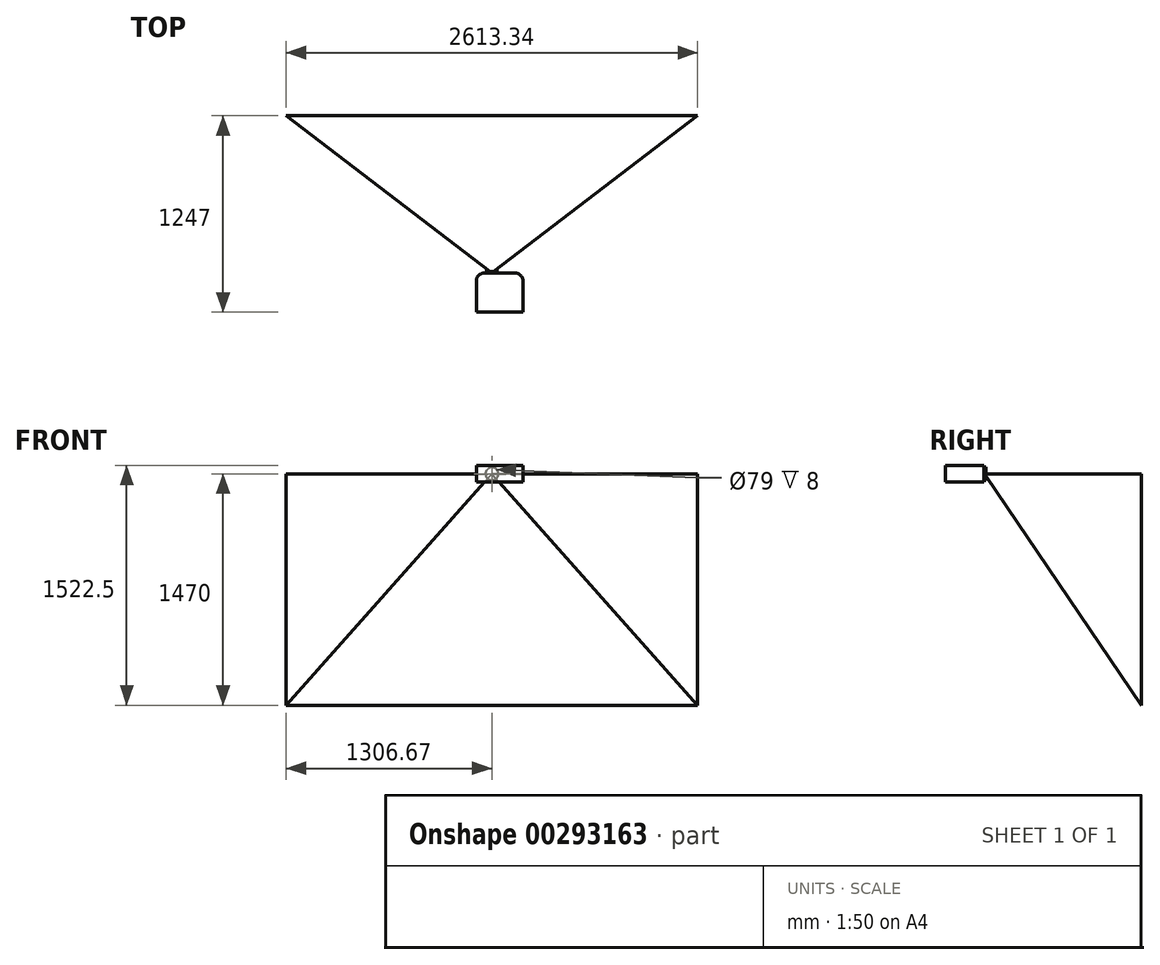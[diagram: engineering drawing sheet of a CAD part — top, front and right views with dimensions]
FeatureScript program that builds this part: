
annotation { "Feature Type Name" : "Feature", "Feature Type Description" : "" }
export const myFeature = defineFeature(function(context is Context, id is Id, definition is map)
    precondition{}
    {
        {
            var Q0;
            Q0=qCreatedBy(makeId("Top.planeOp"),FACE);
            var sketch = newSketch(context, id + "F0", { "sketchPlane" : qUnion([Q0])});
            skLineSegment(sketch, "E0.bottom", {"start": v(-99, 0) * mm, "end": v(198, 0) * mm});
            skLineSegment(sketch, "E0.top", {"start": v(-99, -247) * mm, "end": v(198, -247) * mm});
            skLineSegment(sketch, "E0.left", {"start": v(-99, 0) * mm, "end": v(-99, -247) * mm});
            skLineSegment(sketch, "E0.right", {"start": v(198, 0) * mm, "end": v(198, -247) * mm});
            skSolve(sketch);
        }
        {
            var Q0;
            Q0=makeQuery(id+"F0.imprint","IMPRINT",FACE,{"disambiguationData":[TD([[makeQuery(id+"F0.imprint","IMPRINT",EDGE,{"derivedFrom":sQuery(id+"F0.wireOp",EDGE,"E0.bottom")}),-1.0]])]});
            extrude(context, id + "F1", {"entities" : qUnion([Q0]), "endBound" : BoundingType.SYMMETRIC, "depth" : 105 * mm});
        }
        {
            var Q0;
            Q0=qCreatedBy(makeId("Right.planeOp"),FACE);
            var sketch = newSketch(context, id + "F2", { "sketchPlane" : qUnion([Q0])});
            skLineSegment(sketch, "E1", {"start": v(0, 0) * mm, "end": v(-269.92, 0) * mm, "construction": true});
            skLineSegment(sketch, "E2", {"start": v(0, 0) * mm, "end": v(0, 42.5) * mm});
            skLineSegment(sketch, "E3", {"start": v(0, 42.5) * mm, "end": v(10, 42.5) * mm});
            skLineSegment(sketch, "E4", {"start": v(10, 42.5) * mm, "end": v(10, 39.5) * mm});
            skLineSegment(sketch, "E5", {"start": v(10, 39.5) * mm, "end": v(2, 39.5) * mm});
            skLineSegment(sketch, "E6", {"start": v(0, 0) * mm, "end": v(7.3, 0) * mm});
            skArc(sketch, "E7", {"start": v(7.3, 0) * mm, "mid": v(5.96, 19.93) * mm, "end": v(2, 39.5) * mm});
            skSolve(sketch);
        }
        {
            var Q0;
            Q0=makeQuery(id+"F2.imprint","IMPRINT",FACE,{"disambiguationData":[TD([[makeQuery(id+"F2.imprint","IMPRINT",EDGE,{"derivedFrom":sQuery(id+"F2.wireOp",EDGE,"E2")}),-1.0]])]});
            var Q1;
            Q1=sQuery(id+"F2.wireOp",EDGE,"E1");
            revolve(context, id + "F3", {"operationType" : NewBodyOperationType.ADD, "entities" : qUnion([Q0]), "axis" : qUnion([Q1]), "revolveType" : RevolveType.FULL});
        }
        {
            var Q0;
            Q0=makeQuery(id+"F1.opExtrude","SWEPT_EDGE",EDGE,{"disambiguationData":[OSD([sQuery(id+"F0.wireOp",EDGE,"E0.bottom"),sQuery(id+"F0.wireOp",EDGE,"E0.right")])]});
            var Q1;
            Q1=makeQuery(id+"F1.opExtrude","SWEPT_EDGE",EDGE,{"disambiguationData":[OSD([sQuery(id+"F0.wireOp",EDGE,"E0.bottom"),sQuery(id+"F0.wireOp",EDGE,"E0.left")])]});
            fillet(context, id + "F4", {"entities" : qUnion([Q0, Q1]), "radius" : 50 * mm, "tangentPropagation" : true, "allowEdgeOverflow" : false});
        }
        {
            var Q0;
            Q0=qCreatedBy(makeId("Right.planeOp"),FACE);
            var sketch = newSketch(context, id + "F5", { "sketchPlane" : qUnion([Q0])});
            skLineSegment(sketch, "E8", {"start": v(0, 0) * mm, "end": v(1000, 0) * mm});
            skLineSegment(sketch, "E9", {"start": v(1000, 0) * mm, "end": v(1000, -1470) * mm});
            skLineSegment(sketch, "E10", {"start": v(1000, -1470) * mm, "end": v(0, 0) * mm});
            skPoint(sketch, "E11", {"position": v(1, 0) * mm});
            skPoint(sketch, "E12", {"position": v(1, -1.47) * mm});
            skLineSegment(sketch, "E13", {"start": v(1, 0) * mm, "end": v(1, -1.47) * mm, "construction": true});
            skSolve(sketch);
        }
        {
            var Q0;
            Q0=sQuery(id+"F5.wireOp",EDGE,"E9");
            cPlane(context, id + "F6", {"entities" : qUnion([Q0]), "cplaneType" : CPlaneType.LINE_ANGLE, "offset" : 25 * mm, "angle" : 90 * degree, "width" : 150 * mm, "height" : 150 * mm});
        }
        {
            var Q0;
            Q0=qCreatedBy(id+"F6.planeOp",FACE);
            var sketch = newSketch(context, id + "F7", { "sketchPlane" : qUnion([Q0])});
            skLineSegment(sketch, "E14.bottom", {"start": v(1306.67, 0) * mm, "end": v(-1306.67, 0) * mm});
            skLineSegment(sketch, "E14.top", {"start": v(1306.67, -1470) * mm, "end": v(-1306.67, -1470) * mm});
            skLineSegment(sketch, "E14.left", {"start": v(1306.67, 0) * mm, "end": v(1306.67, -1470) * mm});
            skLineSegment(sketch, "E14.right", {"start": v(-1306.67, 0) * mm, "end": v(-1306.67, -1470) * mm});
            skPoint(sketch, "E14.middle", {"position": v(0, -735) * mm});
            skSolve(sketch);
        }
        {
            var Q1;
            Q1=makeQuery(id+"F7.imprint","IMPRINT",FACE,{"disambiguationData":[TD([[makeQuery(id+"F7.imprint","IMPRINT",EDGE,{"derivedFrom":sQuery(id+"F7.wireOp",EDGE,"E14.bottom")}),1.0]])]});
            var Q2;
            Q2=sQuery(id+"F5.wireOp",VERTEX,"E12");
            loft(context, id + "F8", {"sheetProfilesArray" : [{ "sheetProfileEntities" : qUnion([Q1]) }, { "sheetProfileEntities" : qUnion([Q2]) }]});
        }
    });
